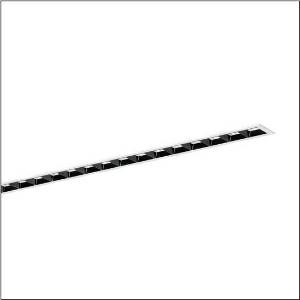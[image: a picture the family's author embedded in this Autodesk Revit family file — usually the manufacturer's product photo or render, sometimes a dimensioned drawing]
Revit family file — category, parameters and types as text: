
# Revit family: silica_r__21_51mx14tat4w_c2be
name_source: partatom
category: Lighting Fixtures
units: mm (PartAtom-declared; Revit-internal decimal feet)

## family parameters
Cut with Voids When Loaded = No
Host = Face
Light Source = No
Part Type = Normal
Room Calculation Point = No
Round Connector Dimension = Use Diameter
Shared = No

## types (1)
- --- (1 x LED, 3280 lm, 32.4 W, 6500K)
    Apparent Load = 32 VA
    CIE Flux Codes = 74 94 99 100 100
    Color Rendering = 80
    Color Temperature = 6500K
    Default Elevation = 1800 mm
    Description = Silica® 21, office luminaire, primary light control with darklight reflector, of PMMA, black, light emission: direct distribution, primary light characteristic: asymmetric, installation type: recessed, LED, rated luminous flux: 3.280lm, luminous efficacy: 96lm/W, light colour: 8tw, colour temperature: 2700..6500K, control gear: DALI DT8, with terminal, 3+2-pole, max. 2.5mm², mains connection: 220..240V, AC, 50/60Hz, rated input power: 34.1W, luminaire housing, of aluminium, traffic white (RAL 9016), length: 1.228mm, width: 79mm, height: 53mm, protection rating (complete): IP20, insulation class (complete): insulation class I (protective earthing), certification: CE, ENEC, VDE, permissible operating ambient temperature: 0..+35°C, standard: EN 50419, packaging unit: 1 piece
    Height = 0 mm  [stored 0 ft]
    Lamp = 1 x LED
    Lamp Light Flux = 3280 lm
    Lamp Power = 32.4 W
    Lamp count = 1
    Length = 1227 mm
    Luminous efficacy = 101 lm/W
    Manufacturer = Siteco
    ModVariant = No
    Model = 51MX14TAT4W
    Mounting Place = Ceiling
    Mounting Type = Recessed
    Number of Poles = 1
    OnlyDefault = Yes
    Power Factor = 1
    Product Name = Silica® 21
    Product group = office luminaire | ceiling recessed
    ProductGroupID = 401
    Protection Class = Protection class I
    Protection Degree = IP 20
    RLX_Detail_Level = 1
    RLX_Emergency_Light_Flux = 0 lm
    RLX_Emergency_Type = 0
    RLX_Emergency_Type_DB = No
    RlxData = <blob elided: 36617 chars, md5=aa134b37>
    Socket = socket
    Standby Power = 0 W
    System Light Flux = 3280 lm
    System Power = 32 W
    Type Comments = individual setting
    Type Image = l_1335880.jpg
    URL = http://relux.com
    VarID = @adj_140034
    Voltage = 0 V
    Weight = 0.00 kg
    Width = 79 mm

note: [stored X ft] marks values corroborated as IEEE doubles in the binary element streams (Revit-internal decimal feet)

## geometry (parser evidence)
native form markers: Blend x4, Sweep x10
no freeform markers — native parametric forms only
